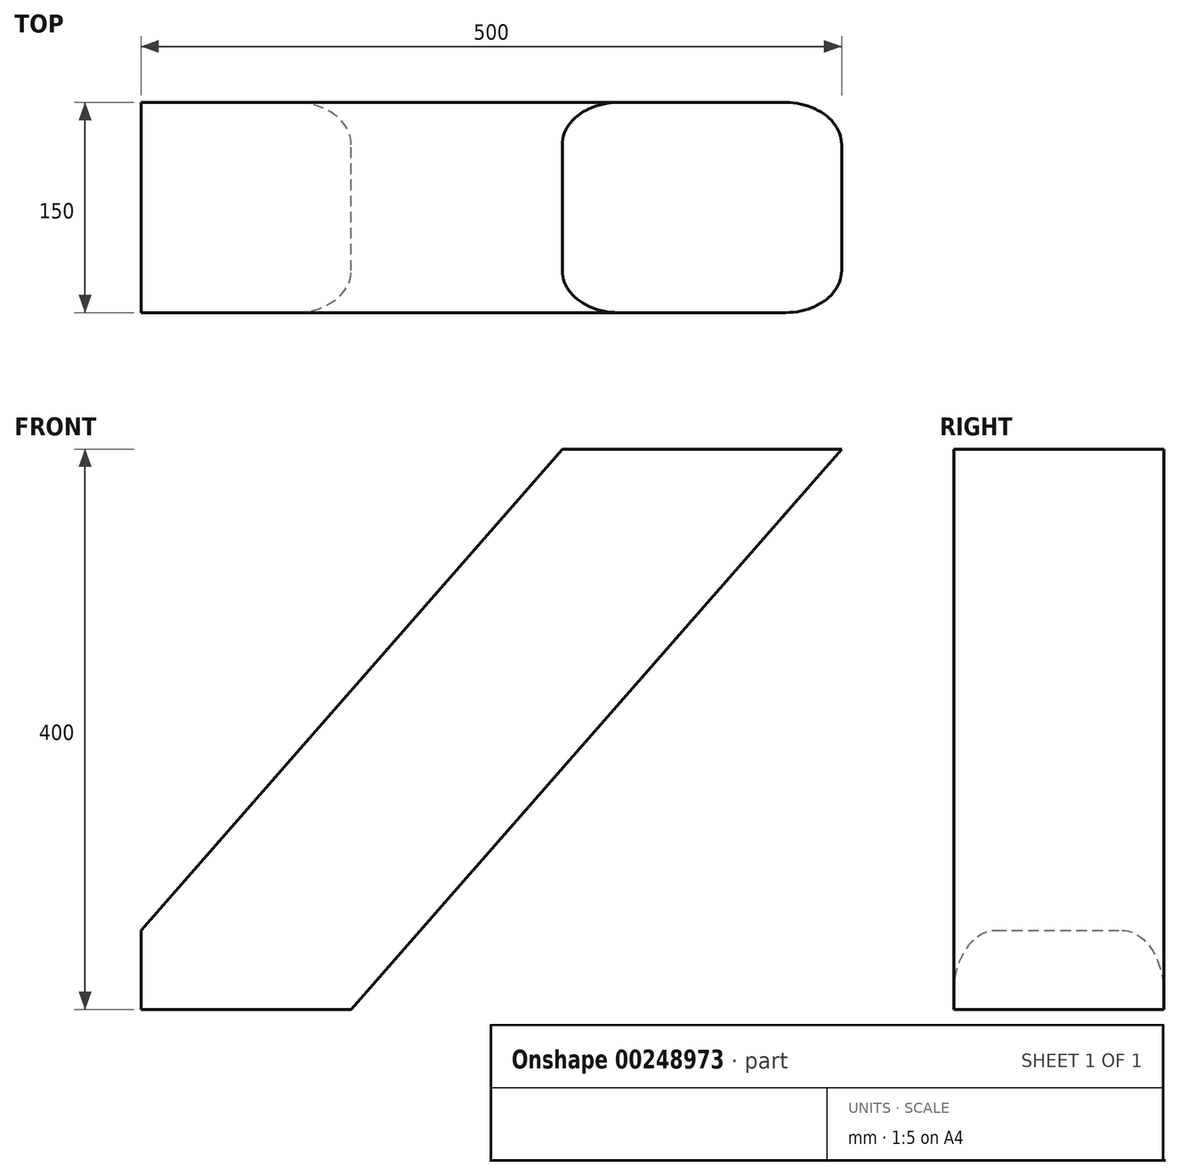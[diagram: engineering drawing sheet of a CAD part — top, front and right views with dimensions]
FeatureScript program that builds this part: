
annotation { "Feature Type Name" : "Feature", "Feature Type Description" : "" }
export const myFeature = defineFeature(function(context is Context, id is Id, definition is map)
    precondition{}
    {
        {
            var Q0;
            Q0=qCreatedBy(makeId("Front.planeOp"),FACE);
            var sketch = newSketch(context, id + "F0", { "sketchPlane" : qUnion([Q0])});
            skLineSegment(sketch, "E0.bottom", {"start": v(0, 0) * mm, "end": v(150, 0) * mm, "construction": true});
            skLineSegment(sketch, "E0.top", {"start": v(0, 150) * mm, "end": v(150, 150) * mm});
            skLineSegment(sketch, "E0.left", {"start": v(0, 0) * mm, "end": v(0, 150) * mm, "construction": true});
            skLineSegment(sketch, "E0.right", {"start": v(150, 0) * mm, "end": v(150, 150) * mm, "construction": true});
            skLineSegment(sketch, "E1.bottom", {"start": v(350, 700) * mm, "end": v(500, 700) * mm, "construction": true});
            skLineSegment(sketch, "E1.top", {"start": v(350, 550) * mm, "end": v(500, 550) * mm});
            skLineSegment(sketch, "E1.left", {"start": v(350, 700) * mm, "end": v(350, 550) * mm, "construction": true});
            skLineSegment(sketch, "E1.right", {"start": v(500, 700) * mm, "end": v(500, 550) * mm, "construction": true});
            skLineSegment(sketch, "E2", {"start": v(150, 150) * mm, "end": v(500, 550) * mm});
            skLineSegment(sketch, "E3", {"start": v(300.68, 550) * mm, "end": v(0, 206.36) * mm});
            skLineSegment(sketch, "E4", {"start": v(500, 550) * mm, "end": v(300.68, 550) * mm});
            skLineSegment(sketch, "E5", {"start": v(0, 150) * mm, "end": v(0, 206.36) * mm});
            skPoint(sketch, "E6.orphan", {"position": v(-49.32, 150) * mm});
            skSolve(sketch);
        }
        {
            var Q0;
            Q0 = qSketchRegion(id + "F0", true);
            extrude(context, id + "F1", {"entities" : qUnion([Q0]), "depth" : 150 * mm});
        }
        {
            var Q0;
            Q0=makeQuery(id+"F1.opExtrude","CAP_EDGE",EDGE,{"disambiguationData":[OSD([sQuery(id+"F0.wireOp",EDGE,"E3")])],"isStart":false});
            var Q1;
            Q1=makeQuery(id+"F1.opExtrude","CAP_EDGE",EDGE,{"disambiguationData":[OSD([sQuery(id+"F0.wireOp",EDGE,"E2")])],"isStart":false});
            var Q2;
            Q2=makeQuery(id+"F1.opExtrude","CAP_EDGE",EDGE,{"disambiguationData":[OSD([sQuery(id+"F0.wireOp",EDGE,"E2")])],"isStart":true});
            var Q3;
            Q3=makeQuery(id+"F1.opExtrude","CAP_EDGE",EDGE,{"disambiguationData":[OSD([sQuery(id+"F0.wireOp",EDGE,"E3")])],"isStart":true});
            fillet(context, id + "F2", {"entities" : qUnion([Q0, Q1, Q2, Q3]), "radius" : 30 * mm, "tangentPropagation" : true, "allowEdgeOverflow" : false});
        }
    });
